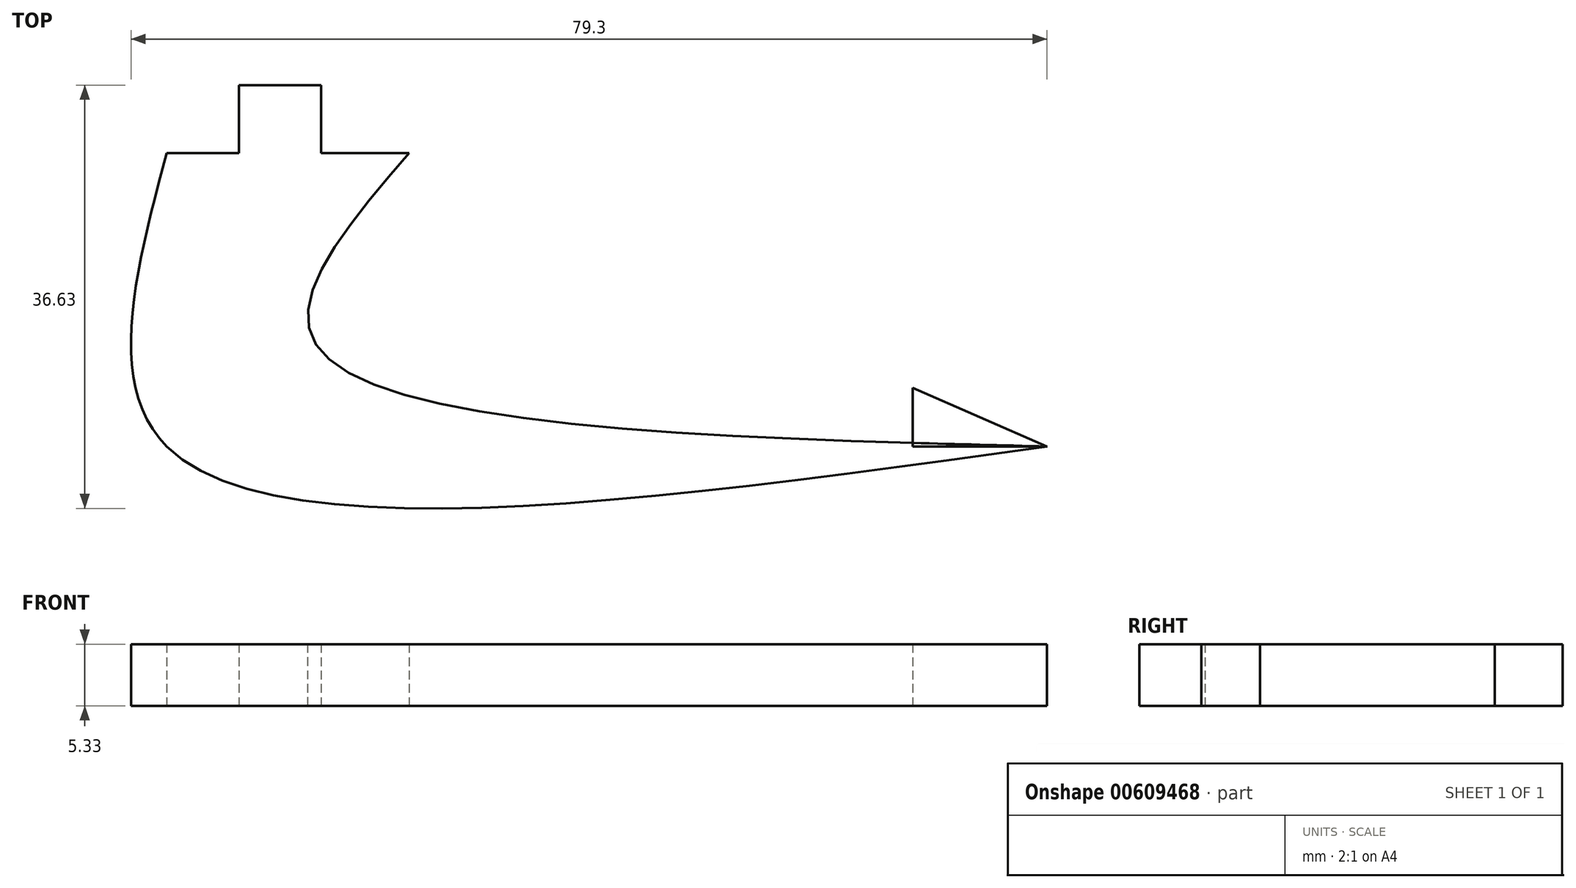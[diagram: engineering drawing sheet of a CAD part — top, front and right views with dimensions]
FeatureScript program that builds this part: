
annotation { "Feature Type Name" : "Feature", "Feature Type Description" : "" }
export const myFeature = defineFeature(function(context is Context, id is Id, definition is map)
    precondition{}
    {
        {
            var Q0;
            Q0=qCreatedBy(makeId("Top.planeOp"),FACE);
            var sketch = newSketch(context, id + "F0", { "sketchPlane" : qUnion([Q0])});
            skLineSegment(sketch, "E0.bottom", {"start": v(2.87, -2.93) * mm, "end": v(-2.87, -2.93) * mm});
            skLineSegment(sketch, "E1", {"start": v(-2.87, -2.93) * mm, "end": v(-10.5, -2.93) * mm});
            skLineSegment(sketch, "E2", {"start": v(2.87, -2.93) * mm, "end": v(10.5, -2.93) * mm});
            skLineSegment(sketch, "E3", {"start": v(-10.5, -2.93) * mm, "end": v(-10.5, -28.33) * mm});
            skLineSegment(sketch, "E4", {"start": v(-10.5, -28.33) * mm, "end": v(65.7, -28.33) * mm});
            skFitSpline(sketch, "E5", {"points": [v(-10.5, -2.93) * mm, v(-10.5, -28.33) * mm, v(65.7, -28.33) * mm], "startDerivative": vector(-22, -82.1) * mm, "endDerivative": vector(158.3, 22) * mm});
            skLineSegment(sketch, "E6", {"start": v(72.23, -28.33) * mm, "end": v(65.7, -28.33) * mm});
            skFitSpline(sketch, "E7", {"points": [v(10.5, -2.93) * mm, v(2.2, -19.15) * mm, v(65.7, -28.33) * mm], "startDerivative": vector(-44.88, -52.32) * mm, "endDerivative": vector(136.85, -3.45) * mm});
            skLineSegment(sketch, "E8", {"start": v(65.7, -28.33) * mm, "end": v(54.07, -23.25) * mm});
            skLineSegment(sketch, "E9", {"start": v(54.07, -23.25) * mm, "end": v(54.07, -28.33) * mm});
            skPoint(sketch, "E10", {"position": v(0, -2.93) * mm});
            skLineSegment(sketch, "E11", {"start": v(0, -2.93) * mm, "end": v(3.81, -2.93) * mm});
            skLineSegment(sketch, "E12", {"start": v(-10.5, -2.93) * mm, "end": v(-4.14, -2.93) * mm});
            skLineSegment(sketch, "E13", {"start": v(-10.5, -2.93) * mm, "end": v(-4.24, -2.93) * mm});
            skLineSegment(sketch, "E14", {"start": v(-4.24, -2.93) * mm, "end": v(-4.24, 2.93) * mm});
            skLineSegment(sketch, "E15", {"start": v(-4.24, 2.93) * mm, "end": v(2.87, 2.93) * mm});
            skLineSegment(sketch, "E16", {"start": v(2.87, 2.93) * mm, "end": v(2.87, -2.93) * mm});
            skSolve(sketch);
        }
        {
            var Q0;
            Q0=makeQuery(id+"F0.imprint","IMPRINT",FACE,{"disambiguationData":[TD([[makeQuery(id+"F0.imprint","IMPRINT",EDGE,{"derivedFrom":sQuery(id+"F0.wireOp",EDGE,"E0.bottom")}),-1.0]])]});
            var Q1;
            Q1=makeQuery(id+"F0.imprint","IMPRINT",FACE,{"disambiguationData":[TD([[makeQuery(id+"F0.imprint","IMPRINT",EDGE,{"derivedFrom":sQuery(id+"F0.wireOp",EDGE,"E0.bottom")}),1.0]])]});
            var Q2;
            {var subQ0=sQuery(id+"F0.wireOp",EDGE,"E3");Q2=makeQuery(id+"F0.imprint","IMPRINT",FACE,{"disambiguationData":[TD([[makeQuery(id+"F0.imprint","IMPRINT",EDGE,{"derivedFrom":subQ0}),-1.0]])]});}
            var Q3;
            {var subQ1=sQuery(id+"F0.wireOp",EDGE,"E4");var subQ3=makeQuery(id+"F0.imprint","INTERSECT",VERTEX,{"derivedFrom":[subQ1,sQuery(id+"F0.wireOp",EDGE,"E9")]});Q3=makeQuery(id+"F0.imprint","IMPRINT",FACE,{"disambiguationData":[TD([[makeQuery(id+"F0.imprint","IMPRINT",EDGE,{"disambiguationData":[TD([[subQ3,1.0]])],"derivedFrom":subQ1}),-1.0]])]});}
            var Q4;
            {var subQ0=sQuery(id+"F0.wireOp",EDGE,"E8");Q4=makeQuery(id+"F0.imprint","IMPRINT",FACE,{"disambiguationData":[TD([[makeQuery(id+"F0.imprint","IMPRINT",EDGE,{"derivedFrom":subQ0}),1.0]])]});}
            extrude(context, id + "F1", {"entities" : qUnion([Q0, Q1, Q2, Q3, Q4]), "depth" : 5.33 * mm, "offsetDistance" : 25.4 * mm});
        }
    });
